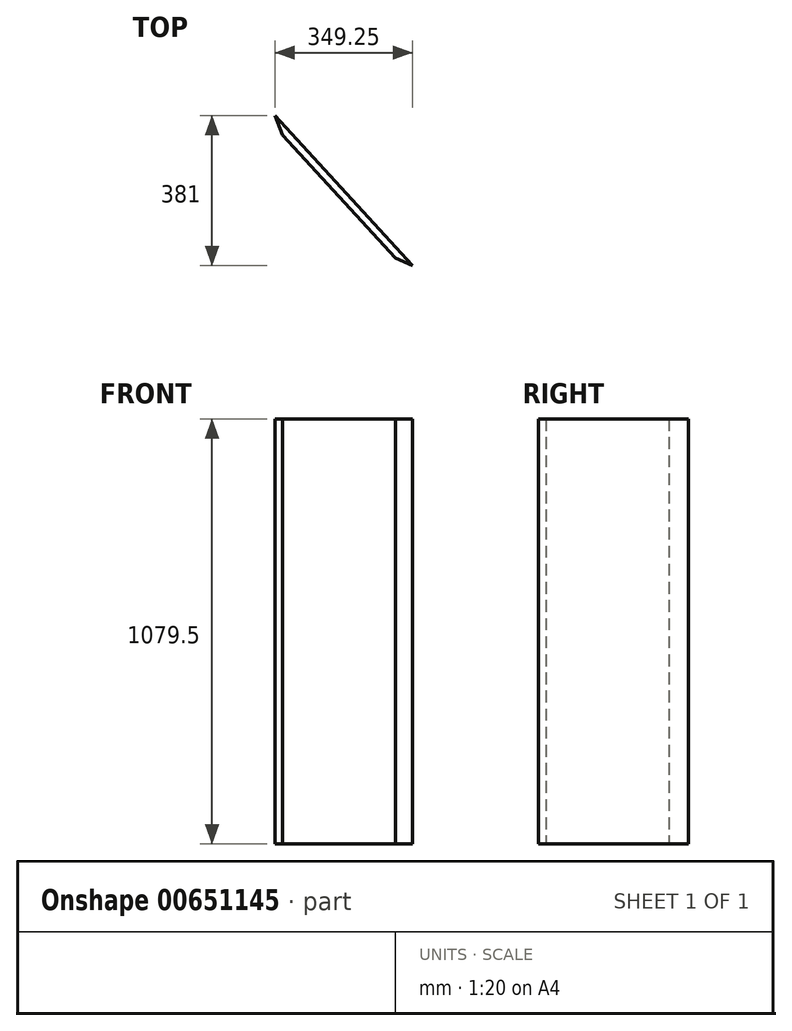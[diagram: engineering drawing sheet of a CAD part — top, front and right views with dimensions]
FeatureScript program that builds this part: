
annotation { "Feature Type Name" : "Feature", "Feature Type Description" : "" }
export const myFeature = defineFeature(function(context is Context, id is Id, definition is map)
    precondition{}
    {
        {
            var Q0;
            Q0=qCreatedBy(makeId("Top.planeOp"),FACE);
            var sketch = newSketch(context, id + "F0", { "sketchPlane" : qUnion([Q0])});
            skLineSegment(sketch, "E0", {"start": v(-168.56, 197.98) * mm, "end": v(180.69, -183.02) * mm});
            skLineSegment(sketch, "E1.trimOffspring", {"start": v(-149.51, 149) * mm, "end": v(137.38, -163.97) * mm});
            skLineSegment(sketch, "E2", {"start": v(-168.56, 197.98) * mm, "end": v(-149.51, 149) * mm});
            skLineSegment(sketch, "E3", {"start": v(137.38, -163.97) * mm, "end": v(180.69, -183.02) * mm});
            skSolve(sketch);
        }
        {
            var Q0;
            Q0=makeQuery(id+"F0.imprint","IMPRINT",FACE,{"disambiguationData":[TD([[makeQuery(id+"F0.imprint","IMPRINT",EDGE,{"derivedFrom":sQuery(id+"F0.wireOp",EDGE,"E0")}),-1.0]])]});
            extrude(context, id + "F1", {"entities" : qUnion([Q0]), "depth" : 1079.5 * mm, "offsetDistance" : 25.4 * mm});
        }
    });
